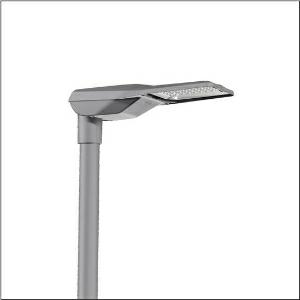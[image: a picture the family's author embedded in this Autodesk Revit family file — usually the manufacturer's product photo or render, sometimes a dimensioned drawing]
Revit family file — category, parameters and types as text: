
# Revit family: streetlight_sl_21_iq_mini___st0_5a_5xe2b41d08hb_2494
name_source: partatom
category: Lighting Fixtures
units: mm (PartAtom-declared; Revit-internal decimal feet)

## family parameters
Cut with Voids When Loaded = No
Host = Face
Light Source = No
Part Type = Normal
Room Calculation Point = No
Round Connector Dimension = Use Diameter
Shared = No

## types (1)
- --- (1 x LED, 9860 lm, 70.9 W, 4000K)
    Apparent Load = 71 VA
    CIE Flux Codes = 41 75 97 100 100
    Color Rendering = 70
    Color Temperature = 4000K
    Default Elevation = 1800 mm
    Description = Streetlight SL 21 iQ mini, mast luminaire, primary light control with lens, of PMMA, primary optical cover: cover, of toughened safety glass, transparent, light distribution: ST0.5a, light emission: direct distribution, primary light characteristic: asymmetric, installation type: post-top, side-entry, LED, High Power LED, rated luminous flux: 9.860lm, luminous efficacy: 139lm/W, light colour: 740, colour temperature: 4000K, control gear: iQ-Comfort, control: Auto-Match, Temp-Guard, Lumen-Switch, Night-Set, Smart-Wire, Light-Fading, Desk-Remote (wireless, voltage-free reading and setting of iQ features in the workshop via application-optimized NFC function/RFID function), optimised constant luminous flux control (CLO 2.0), pre-setting: linear dimming characteristic, mains connection: 220..240V, AC, 50/60Hz, start of lifetime: 71W, end of service life: 75W, reduction: 31W, luminaire housing, of diecast aluminium, powder-coated, Siteco® metallic grey (DB 702S), corrosivity category C5 mid according to DIN EN ISO 12944, please order mast flange separately, inclination adjustable: 0°, 5°, 10°, 15°, sealing non-destructively replaceable, multi-level sealing system, length: 628mm, width: 235mm, height: 110mm, mast flange for spigot size: 42mm (side-entry): 5XC10008XM4, 60/48mm (side-entry/post-top): 5XC10108XM2, 76/60mm (side-entry/post-top): 5XC10108XM1, mounting height: 4..8m, protection rating (complete): IP66, insulation class (complete): insulation class II (safety insulation), certification: CE, ENEC, ENEC+, VDE, impact resistance: IK10, permissible operating ambient temperature for outdoor applications: -40..+50°C, standard-compliant lighting for roads and squares, packaging unit: 1 piece

Light Distribution: ST0.5a
    Height = 110 mm
    Lamp = 1 x LED
    Lamp Light Flux = 9860 lm
    Lamp Power = 70.9 W
    Lamp count = 1
    Length = 625 mm
    Luminous efficacy = 139 lm/W
    Manufacturer = Siteco
    ModVariant = No
    Model = 5XE2B41D08HB
    Number of Poles = 1
    OnlyDefault = Yes
    Power Factor = 1
    Product Name = Streetlight SL 21 iQ mini | ST0.5a
    Product group = mast luminaire | pylon top
    ProductGroupID = 6100
    Protection Class = Protection class II
    Protection Degree = IP 66
    RLX_Detail_Level = 1
    RLX_Emergency_Light_Flux = 0 lm
    RLX_Emergency_Type = 0
    RLX_Emergency_Type_DB = No
    RlxData = <blob elided: 37297 chars, md5=00c2160c>
    Socket = socket
    Standby Power = 0 W
    System Light Flux = 9860 lm
    System Power = 71 W
    Type Comments = factory setting: luminous flux: 100 % | dim-lin: 254 | 711 mA
    Type Image = l_1003519.jpg
    URL = http://relux.com
    VarID = @adj_180009
    Voltage = 0 V
    Weight = 0.00 kg
    Width = 234 mm

## geometry (parser evidence)
native form markers: Blend x4, Sweep x11
no freeform markers — native parametric forms only
